FCSTD DOCUMENT  (FreeCAD 0.14R3702 (Git))
Label: UniversaleCornerbracket
License: CC-BY 3.0
LicenseURL: http://creativecommons.org/licenses/by/3.0/
objects: Sketcher::SketchObject×1
note: 1 computed .brp shape members not serialized (recipe doc carries the construction recipe); baked Part::Feature solids carry a one-line shape summary decoded from their .brp

FEATURE [Sketcher::SketchObject] Sketch
  sketch-geometry (17):
    g0: LineSegment StartX=0 StartY=0 StartZ=0 EndX=60 EndY=0 EndZ=0
    g1: LineSegment StartX=60 StartY=0 StartZ=0 EndX=60 EndY=20 EndZ=0
    g2: LineSegment StartX=60 StartY=20 StartZ=0 EndX=20 EndY=20 EndZ=0
    g3: LineSegment StartX=20 StartY=20 StartZ=0 EndX=20 EndY=60 EndZ=0
    g4: LineSegment StartX=20.0136 StartY=60 StartZ=0 EndX=0.013551 EndY=60 EndZ=0
    g5: LineSegment StartX=0.013551 StartY=0 StartZ=0 EndX=0.013551 EndY=60 EndZ=0
    g6: LineSegment [constr] StartX=10.0136 StartY=0 StartZ=0 EndX=10.0136 EndY=10 EndZ=0
    g7: LineSegment [constr] StartX=10.0136 StartY=10 StartZ=0 EndX=0.013551 EndY=10 EndZ=0
    g8: Circle CenterX=10.0136 CenterY=10 CenterZ=0 NormalX=0 NormalY=0 NormalZ=1 Radius=2.005
    g9: LineSegment [constr] StartX=10.0136 StartY=10 StartZ=0 EndX=30.0136 EndY=10 EndZ=0
    g10: Circle CenterX=30 CenterY=10 CenterZ=0 NormalX=0 NormalY=0 NormalZ=1 Radius=2.005
    g11: LineSegment [constr] StartX=30.0136 StartY=10 StartZ=0 EndX=50.0136 EndY=10 EndZ=0
    g12: Circle CenterX=50.0136 CenterY=10 CenterZ=0 NormalX=0 NormalY=0 NormalZ=1 Radius=2.005
    g13: LineSegment [constr] StartX=10 StartY=13.1552 StartZ=0 EndX=10 EndY=33.1552 EndZ=0
    g14: Circle CenterX=10 CenterY=33.1552 CenterZ=0 NormalX=0 NormalY=0 NormalZ=1 Radius=2.005
    g15: LineSegment [constr] StartX=10 StartY=33.1552 StartZ=0 EndX=10 EndY=53.1552 EndZ=0
    g16: Circle CenterX=10 CenterY=53.1552 CenterZ=0 NormalX=0 NormalY=0 NormalZ=1 Radius=2.005
  constraints (41):
    c: Coincident(g0,g-1)
    c: PointOnObject(g0,g-1)
    c: Coincident(g1,g0)
    c: Vertical(g1)
    c: Coincident(g2,g1)
    c: Coincident(g3,g2)
    c: Horizontal(g4)
    c: Coincident(g5,g4)
    c: Vertical(g5)
    c: DistanceY(g5) = 60
    c: DistanceY(g1) = 20
    c: DistanceX(g4) = -20
    c: PointOnObject(g6,g0)
    c: Vertical(g6)
    c: DistanceY(g6) = 10
    c: PointOnObject(g7,g6)
    c: PointOnObject(g7,g5)
    c: Horizontal(g7)
    c: DistanceX(g7) = -10
    c: Coincident(g8,g6)
    c: Radius(g8) = 2.005
    c: Coincident(g9,g6)
    c: Horizontal(g9)
    c: DistanceX(g9) = 20
    c: Radius(g10) = 2.005
    c: Coincident(g11,g9)
    c: Horizontal(g11)
    c: DistanceX(g11) = 20
    c: Coincident(g12,g11)
    c: Radius(g12) = 2.005
    c: DistanceY(g13) = 20
    c: Coincident(g14,g13)
    c: Radius(g14) = 2.005
    c: DistanceX(g0) = 60
    c: Coincident(g15,g13)
    c: DistanceY(g15) = 20
    c: Coincident(g16,g15)
    c: Radius(g16) = 2.005
    c: Equal(g5,g0)
    c: Equal(g3,g2)
    c: Equal(g1,g4)
